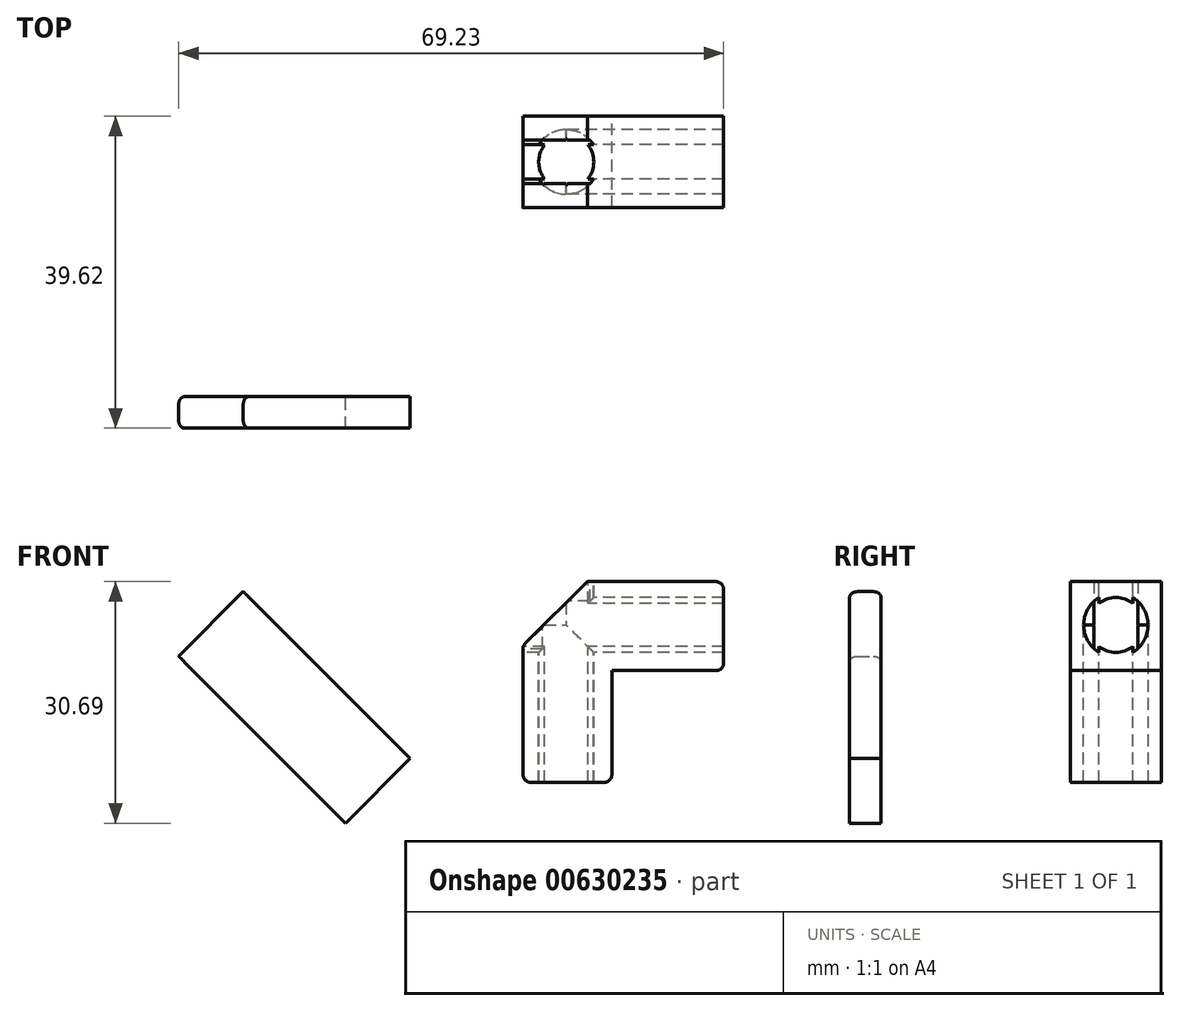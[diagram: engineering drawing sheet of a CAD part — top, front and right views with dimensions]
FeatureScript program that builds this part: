
annotation { "Feature Type Name" : "Feature", "Feature Type Description" : "" }
export const myFeature = defineFeature(function(context is Context, id is Id, definition is map)
    precondition{}
    {
        {
            assignVariable(context, id + "F0", {"name" : "DA", "anyValue" : 7.6});
        }
        {
            assignVariable(context, id + "F1", {"name" : "DH", "anyValue" : 50});
        }
        {
            assignVariable(context, id + "F2", {"name" : "H", "anyValue" : 6});
        }
        {
            assignVariable(context, id + "F3", {"name" : "T", "anyValue" : 2});
        }
        {
            assignVariable(context, id + "F4", {"name" : "WE", "anyValue" : 1.4});
        }
        {
            assignVariable(context, id + "F5", {"name" : "LE", "anyValue" : 60});
        }
        {
            var Q0;
            Q0=qCreatedBy(makeId("Top.planeOp"),FACE);
            var sketch = newSketch(context, id + "F6", { "sketchPlane" : qUnion([Q0])});
            skCircle(sketch, "E0", {"center": v(0, 0) * mm, "radius": 20 * mm});
            skCircle(sketch, "E1", {"center": v(0, 0) * mm, "radius": 3.8 * mm});
            skPoint(sketch, "E2", {"position": v(45, 0) * mm});
            skLineSegment(sketch, "E3", {"start": v(45, -11.85) * mm, "end": v(45, 11.85) * mm, "construction": true});
            skSolve(sketch);
        }
        {
            var Q0;
            Q0=makeQuery(id+"F6.imprint","IMPRINT",FACE,{"disambiguationData":[TD([[makeQuery(id+"F6.imprint","IMPRINT",EDGE,{"derivedFrom":sQuery(id+"F6.wireOp",EDGE,"E0")}),1.0]])]});
            extrude(context, id + "F7", {"entities" : qUnion([Q0]), "endBound" : BoundingType.SYMMETRIC, "depth" : 3 * getVariable(context, 'H') * mm, "offsetDistance" : 25 * mm});
        }
        {
            var Q0;
            Q0=makeQuery(id+"F7.opExtrude","SWEPT_BODY",BODY,{"disambiguationData":[OSD([sQuery(id+"F6.wireOp",EDGE,"E0"),sQuery(id+"F6.wireOp",EDGE,"E1")])]});
            var Q1;
            Q1=sQuery(id+"F6.wireOp",EDGE,"E3");
            circularPattern(context, id + "F8", {"entities" : qUnion([Q0]), "axis" : qUnion([Q1]), "angle" : 360 * degree, "instanceCount" : 4, "equalSpace" : true});
        }
        {
            var Q0;
            Q0=qCreatedBy(makeId("Front.planeOp"),FACE);
            var sketch = newSketch(context, id + "F9", { "sketchPlane" : qUnion([Q0])});
            skPoint(sketch, "E4.0", {"position": v(45, 0) * mm});
            skLineSegment(sketch, "E5.bottom", {"start": v(36, -9) * mm, "end": v(54, -9) * mm, "construction": true});
            skLineSegment(sketch, "E5.top", {"start": v(36, 9) * mm, "end": v(54, 9) * mm, "construction": true});
            skLineSegment(sketch, "E5.left", {"start": v(36, -9) * mm, "end": v(36, 9) * mm, "construction": true});
            skLineSegment(sketch, "E5.right", {"start": v(54, -9) * mm, "end": v(54, 9) * mm, "construction": true});
            skLineSegment(sketch, "E6", {"start": v(16, 29) * mm, "end": v(74, 29) * mm, "construction": true});
            skPoint(sketch, "E7", {"position": v(45, 29) * mm});
            skLineSegment(sketch, "E8", {"start": v(16, 45) * mm, "end": v(74, 45) * mm, "construction": true});
            skPoint(sketch, "E9", {"position": v(45, 45) * mm});
            skLineSegment(sketch, "E10", {"start": v(45, 0) * mm, "end": v(0, 45) * mm, "construction": true});
            skCircle(sketch, "E11", {"center": v(0, 45) * mm, "radius": 3.8 * mm, "construction": true});
            skLineSegment(sketch, "E12", {"start": v(0, 45) * mm, "end": v(-7.03, 52.03) * mm, "construction": true});
            skPoint(sketch, "E13", {"position": v(19.5, 29) * mm});
            skLineSegment(sketch, "E14", {"start": v(19.5, 29) * mm, "end": v(70.5, 29) * mm});
            skLineSegment(sketch, "E15", {"start": v(70.5, 29) * mm, "end": v(70.5, 32.5) * mm});
            skLineSegment(sketch, "E16", {"start": v(70.5, 32.5) * mm, "end": v(19.5, 32.5) * mm});
            skLineSegment(sketch, "E17", {"start": v(19.5, 32.5) * mm, "end": v(19.5, 29) * mm});
            skLineSegment(sketch, "E18", {"start": v(36, 29) * mm, "end": v(36, 23.2) * mm});
            skLineSegment(sketch, "E19", {"start": v(36, 23.2) * mm, "end": v(21.8, 23.2) * mm});
            skLineSegment(sketch, "E20", {"start": v(21.8, 23.2) * mm, "end": v(21.8, 9) * mm});
            skLineSegment(sketch, "E21", {"start": v(21.8, 9) * mm, "end": v(16, 9) * mm});
            skLineSegment(sketch, "E22", {"start": v(36, 32.5) * mm, "end": v(36, 34.5) * mm});
            skLineSegment(sketch, "E23", {"start": v(36, 34.5) * mm, "end": v(10.5, 34.5) * mm});
            skLineSegment(sketch, "E24", {"start": v(10.5, 34.5) * mm, "end": v(10.5, 9) * mm});
            skLineSegment(sketch, "E25", {"start": v(10.5, 9) * mm, "end": v(12.5, 9) * mm});
            skLineSegment(sketch, "E26", {"start": v(12.5, 9) * mm, "end": v(16, 9) * mm});
            skLineSegment(sketch, "E27", {"start": v(36, 29) * mm, "end": v(36, 32.5) * mm});
            skLineSegment(sketch, "E28", {"start": v(16, 29) * mm, "end": v(19.5, 32.5) * mm});
            skLineSegment(sketch, "E29", {"start": v(16, 29) * mm, "end": v(19.5, 29) * mm});
            skLineSegment(sketch, "E30", {"start": v(70.5, 29) * mm, "end": v(74, 29) * mm});
            skLineSegment(sketch, "E31", {"start": v(74, 29) * mm, "end": v(70.5, 32.5) * mm});
            skLineSegment(sketch, "E32", {"start": v(10.5, 26.33) * mm, "end": v(18.67, 34.5) * mm});
            skPoint(sketch, "E33", {"position": v(14.59, 30.41) * mm});
            skSolve(sketch);
        }
        {
            var Q0;
            {var subQ0=sQuery(id+"F9.wireOp",EDGE,"E17");Q0=makeQuery(id+"F9.imprint","IMPRINT",FACE,{"disambiguationData":[TD([[makeQuery(id+"F9.imprint","IMPRINT",EDGE,{"derivedFrom":subQ0}),1.0]])]});}
            var Q1;
            {var subQ0=sQuery(id+"F9.wireOp",EDGE,"E15");Q1=makeQuery(id+"F9.imprint","IMPRINT",FACE,{"disambiguationData":[TD([[makeQuery(id+"F9.imprint","IMPRINT",EDGE,{"derivedFrom":subQ0}),1.0]])]});}
            var Q2;
            Q2=makeQuery(id+"F9.imprint","IMPRINT",FACE,{"disambiguationData":[TD([[makeQuery(id+"F9.imprint","IMPRINT",EDGE,{"derivedFrom":sQuery(id+"F9.wireOp",EDGE,"E17")}),-1.0]])]});
            var Q3;
            Q3=makeQuery(id+"F9.imprint","IMPRINT",FACE,{"disambiguationData":[TD([[makeQuery(id+"F9.imprint","IMPRINT",EDGE,{"derivedFrom":sQuery(id+"F9.wireOp",EDGE,"E15")}),-1.0]])]});
            var Q4;
            Q4=sQuery(id+"F9.wireOp",EDGE,"E6");
            revolve(context, id + "F10", {"entities" : qUnion([Q0, Q1, Q2, Q3]), "axis" : qUnion([Q4]), "revolveType" : RevolveType.FULL});
        }
        {
            var Q0;
            Q0=makeQuery(id+"F10.opRevolve","SWEPT_BODY",BODY,{"disambiguationData":[OSD([sQuery(id+"F9.wireOp",EDGE,"E14"),sQuery(id+"F9.wireOp",EDGE,"E15"),sQuery(id+"F9.wireOp",EDGE,"E16"),sQuery(id+"F9.wireOp",EDGE,"E17")])]});
            transform(context, id + "F11", {"entities" : qUnion([Q0]), "transformType" : TransformType.TRANSLATION_3D, "dx" : 0 * mm, "dy" : 0 * mm, "dz" : (getVariable(context, 'DH') - 3 * getVariable(context, 'H')) / 2 * mm, "makeCopy" : false});
        }
        {
            var Q0;
            {var subQ1=sQuery(id+"F9.wireOp",EDGE,"E17");Q0=makeQuery(id+"F9.imprint","IMPRINT",FACE,{"disambiguationData":[TD([[makeQuery(id+"F9.imprint","IMPRINT",EDGE,{"derivedFrom":subQ1}),-1.0]])]});}
            var Q1;
            {var subQ0=sQuery(id+"F9.wireOp",EDGE,"E17");Q1=makeQuery(id+"F9.imprint","IMPRINT",FACE,{"disambiguationData":[TD([[makeQuery(id+"F9.imprint","IMPRINT",EDGE,{"derivedFrom":subQ0}),1.0]])]});}
            var Q2;
            {var subQ5=sQuery(id+"F9.wireOp",EDGE,"E18");Q2=makeQuery(id+"F9.imprint","IMPRINT",FACE,{"disambiguationData":[TD([[makeQuery(id+"F9.imprint","IMPRINT",EDGE,{"derivedFrom":subQ5}),-1.0]])]});}
            extrude(context, id + "F12", {"entities" : qUnion([Q0, Q1, Q2]), "endBound" : BoundingType.SYMMETRIC, "depth" : (getVariable(context, 'DA') + 2 * 2) * mm, "offsetDistance" : 25 * mm});
        }
        {
            var Q0;
            Q0=makeQuery(id+"F12.opExtrude","SWEPT_BODY",BODY,{"disambiguationData":[OSD([sQuery(id+"F9.wireOp",EDGE,"E18"),sQuery(id+"F9.wireOp",EDGE,"E19"),sQuery(id+"F9.wireOp",EDGE,"E20"),sQuery(id+"F9.wireOp",EDGE,"E21"),sQuery(id+"F9.wireOp",EDGE,"E22"),sQuery(id+"F9.wireOp",EDGE,"E23"),sQuery(id+"F9.wireOp",EDGE,"E24"),sQuery(id+"F9.wireOp",EDGE,"E25"),sQuery(id+"F9.wireOp",EDGE,"E26"),sQuery(id+"F9.wireOp",EDGE,"E27")])]});
            transform(context, id + "F13", {"entities" : qUnion([Q0]), "transformType" : TransformType.TRANSLATION_3D, "dx" : -(getVariable(context, 'DH') - 3 * getVariable(context, 'H')) / 2 * mm, "dy" : 0 * mm, "dz" : (getVariable(context, 'DH') - 3 * getVariable(context, 'H')) / 2 * mm, "makeCopy" : false});
        }
        {
            var Q0;
            Q0=qCreatedBy(makeId("Front.planeOp"),FACE);
            var sketch = newSketch(context, id + "F14", { "sketchPlane" : qUnion([Q0])});
            skLineSegment(sketch, "E34", {"start": v(43, 41.5) * mm, "end": v(47, 41.5) * mm});
            skPoint(sketch, "E35", {"position": v(45, 41.5) * mm});
            skLineSegment(sketch, "E36", {"start": v(45, 41.5) * mm, "end": v(45, 40.7) * mm, "construction": true});
            skArc(sketch, "E37", {"start": v(43, 41.5) * mm, "mid": v(45, 40.7) * mm, "end": v(47, 41.5) * mm});
            skLineSegment(sketch, "E38", {"start": v(70.5, 41.5) * mm, "end": v(19.5, 41.5) * mm, "construction": true});
            skLineSegment(sketch, "E39", {"start": v(19.5, 48.5) * mm, "end": v(70.5, 48.5) * mm, "construction": true});
            skLineSegment(sketch, "E40", {"start": v(45, 41.5) * mm, "end": v(45, 48.5) * mm, "construction": true});
            skPoint(sketch, "E41", {"position": v(45, 45) * mm});
            skLineSegment(sketch, "E42", {"start": v(45, 45) * mm, "end": v(39.35, 45) * mm, "construction": true});
            skSolve(sketch);
        }
        {
            var Q0;
            Q0=makeQuery(id+"F14.imprint","IMPRINT",FACE,{"disambiguationData":[TD([[makeQuery(id+"F14.imprint","IMPRINT",EDGE,{"derivedFrom":sQuery(id+"F14.wireOp",EDGE,"E34")}),-1.0]])]});
            var Q1;
            Q1=sQuery(id+"F14.wireOp",EDGE,"E42");
            revolve(context, id + "F15", {"operationType" : NewBodyOperationType.ADD, "entities" : qUnion([Q0]), "axis" : qUnion([Q1]), "revolveType" : RevolveType.FULL});
        }
        {
            var Q0;
            Q0=qCreatedBy(makeId("Right.planeOp"),FACE);
            var sketch = newSketch(context, id + "F16", { "sketchPlane" : qUnion([Q0])});
            skLineSegment(sketch, "E43.0.0", {"start": v(5.8, 39.2) * mm, "end": v(5.8, 50.5) * mm, "construction": true});
            skLineSegment(sketch, "E43.0.1", {"start": v(5.8, 50.5) * mm, "end": v(-5.8, 50.5) * mm, "construction": true});
            skLineSegment(sketch, "E43.0.2", {"start": v(-5.8, 50.5) * mm, "end": v(-5.8, 39.2) * mm, "construction": true});
            skLineSegment(sketch, "E43.0.3", {"start": v(-5.8, 39.2) * mm, "end": v(5.8, 39.2) * mm, "construction": true});
            skCircle(sketch, "E44.0", {"center": v(0, 45) * mm, "radius": 3.5 * mm, "construction": true});
            skLineSegment(sketch, "E45.bottom", {"start": v(-2.17, 42.26) * mm, "end": v(2.17, 42.26) * mm, "construction": true});
            skLineSegment(sketch, "E45.top", {"start": v(-2.17, 47.74) * mm, "end": v(2.17, 47.74) * mm, "construction": true});
            skLineSegment(sketch, "E45.left", {"start": v(-2.17, 42.26) * mm, "end": v(-2.17, 47.74) * mm, "construction": true});
            skLineSegment(sketch, "E45.right", {"start": v(2.17, 42.26) * mm, "end": v(2.17, 47.74) * mm, "construction": true});
            skLineSegment(sketch, "E46", {"start": v(2.17, 42.26) * mm, "end": v(0, 45) * mm, "construction": true});
            skLineSegment(sketch, "E47", {"start": v(-2.17, 42.26) * mm, "end": v(-2.17, 47.74) * mm});
            skArc(sketch, "E48", {"start": v(-2.17, 47.74) * mm, "mid": v(0, 48.5) * mm, "end": v(2.17, 47.74) * mm});
            skLineSegment(sketch, "E49", {"start": v(2.17, 47.74) * mm, "end": v(2.17, 42.26) * mm});
            skArc(sketch, "E50", {"start": v(2.17, 42.26) * mm, "mid": v(0, 41.5) * mm, "end": v(-2.17, 42.26) * mm});
            skLineSegment(sketch, "E51", {"start": v(-2.77, 41.98) * mm, "end": v(-2.77, 48.02) * mm});
            skPoint(sketch, "E52", {"position": v(-2.77, 45) * mm});
            skLineSegment(sketch, "E53", {"start": v(2.77, 41.98) * mm, "end": v(2.77, 48.02) * mm});
            skLineSegment(sketch, "E54", {"start": v(2.77, 48.02) * mm, "end": v(-2.77, 48.02) * mm, "construction": true});
            skLineSegment(sketch, "E55", {"start": v(-2.77, 41.98) * mm, "end": v(2.77, 41.98) * mm, "construction": true});
            skPoint(sketch, "E56", {"position": v(0, 48.02) * mm});
            skArc(sketch, "E57", {"start": v(-2.78, 48.02) * mm, "mid": v(0, 49.1) * mm, "end": v(2.78, 48.02) * mm});
            skArc(sketch, "E58", {"start": v(-2.78, 41.98) * mm, "mid": v(0, 40.9) * mm, "end": v(2.78, 41.98) * mm});
            skPoint(sketch, "E59", {"position": v(0, 48.5) * mm});
            skPoint(sketch, "E60", {"position": v(0, 49.1) * mm});
            skArc(sketch, "E61", {"start": v(-2.78, 41.98) * mm, "mid": v(-4.1, 45) * mm, "end": v(-2.78, 48.02) * mm});
            skArc(sketch, "E62", {"start": v(2.78, 48.02) * mm, "mid": v(4.1, 45) * mm, "end": v(2.78, 41.98) * mm});
            skCircle(sketch, "E63", {"center": v(0, 45) * mm, "radius": 4.3 * mm, "construction": true});
            skLineSegment(sketch, "E64", {"start": v(-2.17, 42.26) * mm, "end": v(-2.17, 41.3) * mm});
            skLineSegment(sketch, "E65", {"start": v(-2.17, 47.74) * mm, "end": v(-2.17, 48.7) * mm});
            skLineSegment(sketch, "E66", {"start": v(2.17, 42.26) * mm, "end": v(2.17, 41.3) * mm});
            skLineSegment(sketch, "E67", {"start": v(2.17, 47.74) * mm, "end": v(2.17, 48.7) * mm});
            skArc(sketch, "E68", {"start": v(-2.18, 41.3) * mm, "mid": v(-4.3, 45) * mm, "end": v(-2.18, 48.7) * mm});
            skArc(sketch, "E69", {"start": v(2.18, 41.3) * mm, "mid": v(4.3, 45) * mm, "end": v(2.18, 48.7) * mm});
            skSolve(sketch);
        }
        {
            var Q0;
            Q0=makeQuery(id+"F16.imprint","IMPRINT",FACE,{"disambiguationData":[TD([[makeQuery(id+"F16.imprint","IMPRINT",EDGE,{"derivedFrom":sQuery(id+"F16.wireOp",EDGE,"E53")}),-1.0]])]});
            var Q1;
            Q1=makeQuery(id+"F16.imprint","IMPRINT",FACE,{"disambiguationData":[TD([[makeQuery(id+"F16.imprint","IMPRINT",EDGE,{"derivedFrom":sQuery(id+"F16.wireOp",EDGE,"E51")}),1.0]])]});
            var Q2;
            Q2=makeQuery(id+"F16.imprint","IMPRINT",FACE,{"disambiguationData":[TD([[makeQuery(id+"F16.imprint","IMPRINT",EDGE,{"derivedFrom":sQuery(id+"F16.wireOp",EDGE,"E47")}),1.0]])]});
            var Q3;
            {var subQ4=sQuery(id+"F16.wireOp",EDGE,"E61");Q3=makeQuery(id+"F16.imprint","IMPRINT",FACE,{"disambiguationData":[TD([[makeQuery(id+"F16.imprint","IMPRINT",EDGE,{"derivedFrom":subQ4}),1.0]])]});}
            var Q4;
            {var subQ4=sQuery(id+"F16.wireOp",EDGE,"E62");Q4=makeQuery(id+"F16.imprint","IMPRINT",FACE,{"disambiguationData":[TD([[makeQuery(id+"F16.imprint","IMPRINT",EDGE,{"derivedFrom":subQ4}),1.0]])]});}
            var Q5;
            {var subQ8=sQuery(id+"F16.wireOp",EDGE,"E49");Q5=makeQuery(id+"F16.imprint","IMPRINT",FACE,{"disambiguationData":[TD([[makeQuery(id+"F16.imprint","IMPRINT",EDGE,{"derivedFrom":subQ8}),1.0]])]});}
            extrude(context, id + "F17", {"entities" : qUnion([Q0, Q1, Q2, Q3, Q4, Q5]), "operationType" : NewBodyOperationType.REMOVE, "endBound" : BoundingType.THROUGH_ALL, "depth" : 25 * mm, "offsetDistance" : 25 * mm});
        }
        {
            var Q0;
            Q0=makeQuery(id+"F17.boolean.opBoolean","COPY",FACE,{"derivedFrom":makeQuery(id+"F17.opExtrude","SWEPT_FACE",FACE,{"disambiguationData":[OSD([sQuery(id+"F16.wireOp",EDGE,"E47")])]})});
            var sketch = newSketch(context, id + "F18", { "sketchPlane" : qUnion([Q0])});
            skPoint(sketch, "E70", {"position": v(45, 47.74) * mm});
            skLineSegment(sketch, "E71", {"start": v(45, 42.26) * mm, "end": v(45, 47.74) * mm, "construction": true});
            skPoint(sketch, "E72", {"position": v(45, 45) * mm});
            skLineSegment(sketch, "E73.bottom", {"start": v(54, 43.6) * mm, "end": v(36, 43.6) * mm});
            skLineSegment(sketch, "E73.top", {"start": v(54, 46.4) * mm, "end": v(36, 46.4) * mm});
            skLineSegment(sketch, "E73.left", {"start": v(54, 43.6) * mm, "end": v(54, 46.4) * mm, "construction": true});
            skLineSegment(sketch, "E73.right", {"start": v(36, 43.6) * mm, "end": v(36, 46.4) * mm, "construction": true});
            skArc(sketch, "E74", {"start": v(36, 43.6) * mm, "mid": v(34.6, 45) * mm, "end": v(36, 46.4) * mm});
            skArc(sketch, "E75", {"start": v(54, 43.6) * mm, "mid": v(55.4, 45) * mm, "end": v(54, 46.4) * mm});
            skArc(sketch, "E76", {"start": v(31.59, 45) * mm, "mid": v(31.18, 44.01) * mm, "end": v(30.19, 43.6) * mm});
            skArc(sketch, "E77", {"start": v(31.59, 45) * mm, "mid": v(32.04, 46.95) * mm, "end": v(33.31, 48.5) * mm});
            skLineSegment(sketch, "E78", {"start": v(30.19, 43.6) * mm, "end": v(20.98, 43.6) * mm});
            skArc(sketch, "E79", {"start": v(20.98, 43.6) * mm, "mid": v(19.58, 45) * mm, "end": v(20.98, 46.4) * mm});
            skLineSegment(sketch, "E80", {"start": v(20.98, 46.4) * mm, "end": v(30.19, 46.4) * mm});
            skArc(sketch, "E81", {"start": v(30.19, 46.4) * mm, "mid": v(30.57, 47.5) * mm, "end": v(31.15, 48.5) * mm});
            skPoint(sketch, "E82", {"position": v(19.58, 45) * mm});
            skFitSpline(sketch, "E83.0", {"points": [v(33.05, 28.1) * mm, v(32.15, 29) * mm, v(30.36, 30.8) * mm, v(28.12, 33.08) * mm, v(26.33, 34.9) * mm, v(25, 36.27) * mm, v(23.67, 37.64) * mm, v(22.35, 39.03) * mm, v(21.27, 40.2) * mm, v(20.42, 41.15) * mm, v(19.8, 41.88) * mm, v(19.2, 42.63) * mm, v(18.75, 43.29) * mm, v(18.45, 43.85) * mm, v(18.3, 44.23) * mm, v(18.22, 44.54) * mm, v(18.18, 44.78) * mm, v(18.17, 45.02) * mm, v(18.19, 45.25) * mm, v(18.23, 45.5) * mm, v(18.31, 45.8) * mm, v(18.46, 46.17) * mm, v(18.69, 46.6) * mm, v(19.04, 47.13) * mm, v(19.51, 47.77) * mm, v(20.12, 48.5) * mm, v(20.75, 49.23) * mm, v(21.6, 50.17) * mm, v(22.25, 50.87) * mm, v(22.7, 51.33) * mm], "construction": true});
            skPoint(sketch, "E84", {"position": v(18.18, 45) * mm});
            skLineSegment(sketch, "E85.MirrorCS", {"start": v(59.81, 43.6) * mm, "end": v(69.02, 43.6) * mm});
            skArc(sketch, "E86.MirrorCS", {"start": v(69.02, 43.6) * mm, "mid": v(70.42, 45) * mm, "end": v(69.02, 46.4) * mm});
            skArc(sketch, "E87.MirrorCS", {"start": v(59.81, 46.4) * mm, "mid": v(59.43, 47.5) * mm, "end": v(58.85, 48.5) * mm});
            skArc(sketch, "E88.MirrorCS", {"start": v(58.41, 45) * mm, "mid": v(57.96, 46.95) * mm, "end": v(56.69, 48.5) * mm});
            skArc(sketch, "E89.MirrorCS", {"start": v(58.41, 45) * mm, "mid": v(58.82, 44.01) * mm, "end": v(59.81, 43.6) * mm});
            skLineSegment(sketch, "E90", {"start": v(69.02, 46.4) * mm, "end": v(59.81, 46.4) * mm});
            skLineSegment(sketch, "E91", {"start": v(58.85, 48.5) * mm, "end": v(56.69, 48.5) * mm});
            skLineSegment(sketch, "E92.0", {"start": v(43, 47.74) * mm, "end": v(19.5, 47.74) * mm, "construction": true});
            skLineSegment(sketch, "E93.0", {"start": v(70.5, 47.74) * mm, "end": v(47, 47.74) * mm, "construction": true});
            skLineSegment(sketch, "E94.0", {"start": v(19.5, 42.26) * mm, "end": v(43, 42.26) * mm, "construction": true});
            skLineSegment(sketch, "E95.0", {"start": v(47, 42.26) * mm, "end": v(70.5, 42.26) * mm, "construction": true});
            skLineSegment(sketch, "E96", {"start": v(43, 47.74) * mm, "end": v(47, 47.74) * mm, "construction": true});
            skLineSegment(sketch, "E97", {"start": v(43, 42.26) * mm, "end": v(47, 42.26) * mm, "construction": true});
            skLineSegment(sketch, "E98", {"start": v(45, 45) * mm, "end": v(18.18, 45) * mm, "construction": true});
            skLineSegment(sketch, "E99", {"start": v(20.98, 43.6) * mm, "end": v(20.98, 46.4) * mm, "construction": true});
            skLineSegment(sketch, "E100", {"start": v(36, 43.6) * mm, "end": v(18.59, 43.6) * mm, "construction": true});
            skLineSegment(sketch, "E101", {"start": v(36, 46.4) * mm, "end": v(18.59, 46.4) * mm, "construction": true});
            skLineSegment(sketch, "E102", {"start": v(30.19, 43.6) * mm, "end": v(30.19, 46.4) * mm, "construction": true});
            skPoint(sketch, "E103", {"position": v(31.59, 45) * mm});
            skLineSegment(sketch, "E104", {"start": v(19.5, 48.5) * mm, "end": v(42.7, 48.5) * mm, "construction": true});
            skLineSegment(sketch, "E105", {"start": v(31.15, 48.5) * mm, "end": v(33.31, 48.5) * mm});
            skSolve(sketch);
        }
        {
            var Q0;
            {var subQ1=sQuery(id+"F18.wireOp",EDGE,"E76");Q0=makeQuery(id+"F18.imprint","IMPRINT",FACE,{"disambiguationData":[TD([[makeQuery(id+"F18.imprint","IMPRINT",EDGE,{"derivedFrom":subQ1}),-1.0]])]});}
            var Q1;
            Q1=makeQuery(id+"F18.imprint","IMPRINT",FACE,{"disambiguationData":[TD([[makeQuery(id+"F18.imprint","IMPRINT",EDGE,{"derivedFrom":sQuery(id+"F18.wireOp",EDGE,"E73.bottom")}),-1.0]])]});
            var Q2;
            Q2=makeQuery(id+"F18.imprint","IMPRINT",FACE,{"disambiguationData":[TD([[makeQuery(id+"F18.imprint","IMPRINT",EDGE,{"derivedFrom":sQuery(id+"F18.wireOp",EDGE,"E85.MirrorCS")}),1.0]])]});
            var Q3;
            {var subQ0=sQuery(id+"F18.wireOp",EDGE,"E91");Q3=makeQuery(id+"F18.imprint","IMPRINT",FACE,{"disambiguationData":[TD([[makeQuery(id+"F18.imprint","IMPRINT",EDGE,{"derivedFrom":subQ0}),1.0]])]});}
            var Q4;
            {var subQ0=sQuery(id+"F18.wireOp",EDGE,"E105");Q4=makeQuery(id+"F18.imprint","IMPRINT",FACE,{"disambiguationData":[TD([[makeQuery(id+"F18.imprint","IMPRINT",EDGE,{"derivedFrom":subQ0}),-1.0]])]});}
            extrude(context, id + "F19", {"entities" : qUnion([Q0, Q1, Q2, Q3, Q4]), "operationType" : NewBodyOperationType.REMOVE, "oppositeDirection" : true, "depth" : 25 * mm, "offsetDistance" : 25 * mm});
        }
        {
            var Q0;
            Q0=makeQuery(id+"F16.imprint","IMPRINT",FACE,{"disambiguationData":[TD([[makeQuery(id+"F16.imprint","IMPRINT",EDGE,{"derivedFrom":sQuery(id+"F16.wireOp",EDGE,"E47")}),-1.0]])]});
            var Q1;
            {var subQ0=sQuery(id+"F16.wireOp",EDGE,"E50");Q1=makeQuery(id+"F16.imprint","IMPRINT",FACE,{"disambiguationData":[TD([[makeQuery(id+"F16.imprint","IMPRINT",EDGE,{"derivedFrom":subQ0}),1.0]])]});}
            var Q2;
            {var subQ8=sQuery(id+"F16.wireOp",EDGE,"E47");Q2=makeQuery(id+"F16.imprint","IMPRINT",FACE,{"disambiguationData":[TD([[makeQuery(id+"F16.imprint","IMPRINT",EDGE,{"derivedFrom":subQ8}),1.0]])]});}
            var Q3;
            {var subQ8=sQuery(id+"F16.wireOp",EDGE,"E49");Q3=makeQuery(id+"F16.imprint","IMPRINT",FACE,{"disambiguationData":[TD([[makeQuery(id+"F16.imprint","IMPRINT",EDGE,{"derivedFrom":subQ8}),1.0]])]});}
            var Q4;
            {var subQ0=sQuery(id+"F16.wireOp",EDGE,"E48");Q4=makeQuery(id+"F16.imprint","IMPRINT",FACE,{"disambiguationData":[TD([[makeQuery(id+"F16.imprint","IMPRINT",EDGE,{"derivedFrom":subQ0}),1.0]])]});}
            extrude(context, id + "F20", {"entities" : qUnion([Q0, Q1, Q2, Q3, Q4]), "operationType" : NewBodyOperationType.REMOVE, "endBound" : BoundingType.SYMMETRIC, "depth" : 100 * mm, "offsetDistance" : 25 * mm});
        }
        {
            var Q0;
            Q0=makeQuery(id+"F12.opExtrude","CAP_FACE",FACE,{"disambiguationData":[OSD([sQuery(id+"F9.wireOp",EDGE,"E18"),sQuery(id+"F9.wireOp",EDGE,"E19"),sQuery(id+"F9.wireOp",EDGE,"E20"),sQuery(id+"F9.wireOp",EDGE,"E21"),sQuery(id+"F9.wireOp",EDGE,"E22"),sQuery(id+"F9.wireOp",EDGE,"E23"),sQuery(id+"F9.wireOp",EDGE,"E24"),sQuery(id+"F9.wireOp",EDGE,"E25"),sQuery(id+"F9.wireOp",EDGE,"E26"),sQuery(id+"F9.wireOp",EDGE,"E27"),sQuery(id+"F9.wireOp",EDGE,"E32")])],"isStart":false});
            var sketch = newSketch(context, id + "F21", { "sketchPlane" : qUnion([Q0])});
            skLineSegment(sketch, "E106.0", {"start": v(-5.5, 42.33) * mm, "end": v(2.67, 50.5) * mm, "construction": true});
            skPoint(sketch, "E107.0", {"position": v(5.8, 39.2) * mm});
            skLineSegment(sketch, "E108", {"start": v(5.8, 39.2) * mm, "end": v(-1.41, 46.41) * mm, "construction": true});
            skSolve(sketch);
        }
        {
            var Q0;
            Q0=sQuery(id+"F21.wireOp",EDGE,"E108");
            var Q1;
            Q1=sQuery(id+"F21.wireOp",VERTEX,"E106.0.end");
            cPlane(context, id + "F22", {"entities" : qUnion([Q0, Q1]), "cplaneType" : CPlaneType.LINE_ANGLE, "offset" : 25 * mm, "angle" : 90 * degree, "width" : 150 * mm, "height" : 150 * mm});
        }
        {
            var Q0;
            Q0=makeQuery(id+"F12.opExtrude","SWEPT_BODY",BODY,{"disambiguationData":[OSD([sQuery(id+"F9.wireOp",EDGE,"E18"),sQuery(id+"F9.wireOp",EDGE,"E19"),sQuery(id+"F9.wireOp",EDGE,"E20"),sQuery(id+"F9.wireOp",EDGE,"E21"),sQuery(id+"F9.wireOp",EDGE,"E22"),sQuery(id+"F9.wireOp",EDGE,"E23"),sQuery(id+"F9.wireOp",EDGE,"E24"),sQuery(id+"F9.wireOp",EDGE,"E25"),sQuery(id+"F9.wireOp",EDGE,"E26"),sQuery(id+"F9.wireOp",EDGE,"E27"),sQuery(id+"F9.wireOp",EDGE,"E32")])]});
            var Q1;
            Q1=qCreatedBy(id+"F22.planeOp",FACE);
            mirror(context, id + "F23", {"operationType" : NewBodyOperationType.INTERSECT, "entities" : qUnion([Q0]), "mirrorPlane" : qUnion([Q1])});
        }
        {
            var Q0;
            Q0=makeQuery(id+"F17.boolean.opBoolean","COPY",FACE,{"derivedFrom":makeQuery(id+"F17.opExtrude","SWEPT_FACE",FACE,{"disambiguationData":[OSD([sQuery(id+"F16.wireOp",EDGE,"E47"),sQuery(id+"F16.wireOp",EDGE,"E64"),sQuery(id+"F16.wireOp",EDGE,"E65")])]})});
            var sketch = newSketch(context, id + "F24", { "sketchPlane" : qUnion([Q0])});
            skPoint(sketch, "E109.0", {"position": v(45, 45) * mm});
            skFitSpline(sketch, "E110.0", {"points": [v(33.05, 28.1) * mm, v(32.15, 29) * mm, v(30.36, 30.8) * mm, v(28.12, 33.08) * mm, v(26.33, 34.9) * mm, v(25, 36.27) * mm, v(23.67, 37.64) * mm, v(22.35, 39.03) * mm, v(21.27, 40.2) * mm, v(20.42, 41.15) * mm, v(19.8, 41.88) * mm, v(19.2, 42.63) * mm, v(18.75, 43.29) * mm, v(18.45, 43.85) * mm, v(18.3, 44.23) * mm, v(18.22, 44.54) * mm, v(18.18, 44.78) * mm, v(18.17, 45.02) * mm, v(18.19, 45.25) * mm, v(18.23, 45.5) * mm, v(18.31, 45.8) * mm, v(18.46, 46.17) * mm, v(18.69, 46.6) * mm, v(19.04, 47.13) * mm, v(19.51, 47.77) * mm, v(20.12, 48.5) * mm, v(20.75, 49.23) * mm, v(21.6, 50.17) * mm, v(22.25, 50.87) * mm, v(22.7, 51.33) * mm], "construction": true});
            skArc(sketch, "E111.0", {"start": v(20.98, 43.6) * mm, "mid": v(19.58, 45) * mm, "end": v(20.98, 46.4) * mm, "construction": true});
            skArc(sketch, "E112.0", {"start": v(69.02, 43.6) * mm, "mid": v(70.42, 45) * mm, "end": v(69.02, 46.4) * mm, "construction": true});
            skFitSpline(sketch, "E113.0", {"points": [v(56.95, 28.1) * mm, v(57.85, 29) * mm, v(59.64, 30.8) * mm, v(61.88, 33.08) * mm, v(63.67, 34.9) * mm, v(65, 36.27) * mm, v(66.33, 37.64) * mm, v(67.65, 39.03) * mm, v(68.73, 40.2) * mm, v(69.58, 41.15) * mm, v(70.2, 41.88) * mm, v(70.8, 42.63) * mm, v(71.25, 43.29) * mm, v(71.55, 43.85) * mm, v(71.7, 44.23) * mm, v(71.78, 44.54) * mm, v(71.82, 44.78) * mm, v(71.83, 45.02) * mm, v(71.81, 45.25) * mm, v(71.77, 45.5) * mm, v(71.69, 45.8) * mm, v(71.54, 46.17) * mm, v(71.31, 46.6) * mm, v(70.96, 47.13) * mm, v(70.49, 47.77) * mm, v(69.88, 48.5) * mm, v(69.25, 49.23) * mm, v(68.4, 50.17) * mm, v(67.75, 50.87) * mm, v(67.3, 51.33) * mm], "construction": true});
            skLineSegment(sketch, "E114.bottom", {"start": v(70.24, 44.3) * mm, "end": v(74, 44.3) * mm});
            skLineSegment(sketch, "E114.top", {"start": v(70.24, 45.7) * mm, "end": v(74, 45.7) * mm});
            skLineSegment(sketch, "E114.left", {"start": v(70.24, 44.3) * mm, "end": v(70.24, 45.7) * mm});
            skLineSegment(sketch, "E114.right", {"start": v(74, 44.3) * mm, "end": v(74, 45.7) * mm});
            skPoint(sketch, "E115", {"position": v(70.24, 45) * mm});
            skLineSegment(sketch, "E116.0", {"start": v(45, 42.26) * mm, "end": v(45, 47.74) * mm, "construction": true});
            skLineSegment(sketch, "E117.MirrorCS", {"start": v(19.76, 44.3) * mm, "end": v(16, 44.3) * mm});
            skLineSegment(sketch, "E118.MirrorCS", {"start": v(16, 44.3) * mm, "end": v(16, 45.7) * mm});
            skLineSegment(sketch, "E119.MirrorCS", {"start": v(19.76, 45.7) * mm, "end": v(16, 45.7) * mm});
            skLineSegment(sketch, "E120.MirrorCS", {"start": v(19.76, 44.3) * mm, "end": v(19.76, 45.7) * mm});
            skPoint(sketch, "E121.0", {"position": v(74, 45) * mm});
            skSolve(sketch);
        }
        {
            var Q0;
            {var subQ0=sQuery(id+"F24.wireOp",EDGE,"E117.MirrorCS");var subQ4=sQuery(id+"F24.wireOp",EDGE,"E120.MirrorCS");var subQ6=makeQuery(id+"F19.boolean.opBoolean","COPY",EDGE,{"derivedFrom":makeQuery(id+"F19.opExtrude","CAP_EDGE",EDGE,{"disambiguationData":[OSD([sQuery(id+"F18.wireOp",EDGE,"E79")])],"isStart":true})});var subQ9=makeQuery(id+"F24.imprint","INTERSECT",VERTEX,{"derivedFrom":[subQ6,subQ0,subQ4]});Q0=makeQuery(id+"F24.imprint","IMPRINT",FACE,{"disambiguationData":[TD([[makeQuery(id+"F24.imprint","IMPRINT",EDGE,{"disambiguationData":[TD([[subQ9,-1.0]])],"derivedFrom":subQ6}),1.0]])]});}
            var Q1;
            {var subQ0=sQuery(id+"F24.wireOp",EDGE,"E120.MirrorCS");Q1=makeQuery(id+"F24.imprint","IMPRINT",FACE,{"disambiguationData":[TD([[makeQuery(id+"F24.imprint","IMPRINT",EDGE,{"derivedFrom":subQ0}),1.0]])]});}
            var Q2;
            {var subQ0=sQuery(id+"F24.wireOp",EDGE,"E114.bottom");var subQ4=sQuery(id+"F24.wireOp",EDGE,"E114.left");var subQ6=makeQuery(id+"F19.boolean.opBoolean","COPY",EDGE,{"derivedFrom":makeQuery(id+"F19.opExtrude","CAP_EDGE",EDGE,{"disambiguationData":[OSD([sQuery(id+"F18.wireOp",EDGE,"E86.MirrorCS")])],"isStart":true})});var subQ9=makeQuery(id+"F24.imprint","INTERSECT",VERTEX,{"derivedFrom":[subQ6,subQ0,subQ4]});Q2=makeQuery(id+"F24.imprint","IMPRINT",FACE,{"disambiguationData":[TD([[makeQuery(id+"F24.imprint","IMPRINT",EDGE,{"disambiguationData":[TD([[subQ9,-1.0]])],"derivedFrom":subQ6}),-1.0]])]});}
            var Q3;
            {var subQ0=sQuery(id+"F24.wireOp",EDGE,"E114.left");Q3=makeQuery(id+"F24.imprint","IMPRINT",FACE,{"disambiguationData":[TD([[makeQuery(id+"F24.imprint","IMPRINT",EDGE,{"derivedFrom":subQ0}),-1.0]])]});}
            var Q4;
            {var subQ0=sQuery(id+"F24.wireOp",EDGE,"E114.right");Q4=makeQuery(id+"F24.imprint","IMPRINT",FACE,{"disambiguationData":[TD([[makeQuery(id+"F24.imprint","IMPRINT",EDGE,{"derivedFrom":subQ0}),1.0]])]});}
            var Q5;
            {var subQ0=sQuery(id+"F24.wireOp",EDGE,"E118.MirrorCS");Q5=makeQuery(id+"F24.imprint","IMPRINT",FACE,{"disambiguationData":[TD([[makeQuery(id+"F24.imprint","IMPRINT",EDGE,{"derivedFrom":subQ0}),-1.0]])]});}
            extrude(context, id + "F25", {"entities" : qUnion([Q0, Q1, Q2, Q3, Q4, Q5]), "operationType" : NewBodyOperationType.REMOVE, "oppositeDirection" : true, "depth" : getVariable(context, 'WE') * mm, "offsetDistance" : 25 * mm});
        }
        {
            var Q0;
            Q0=makeQuery(id+"F17.boolean.opBoolean","COPY",FACE,{"derivedFrom":makeQuery(id+"F17.opExtrude","SWEPT_FACE",FACE,{"disambiguationData":[OSD([sQuery(id+"F16.wireOp",EDGE,"E49"),sQuery(id+"F16.wireOp",EDGE,"E66"),sQuery(id+"F16.wireOp",EDGE,"E67")])]})});
            var sketch = newSketch(context, id + "F26", { "sketchPlane" : qUnion([Q0])});
            skLineSegment(sketch, "E122.0.0", {"start": v(-17.04, 44.3) * mm, "end": v(-19.76, 44.3) * mm});
            skArc(sketch, "E122.0.1", {"start": v(-19.76, 44.3) * mm, "mid": v(-19.58, 45) * mm, "end": v(-19.76, 45.7) * mm});
            skLineSegment(sketch, "E122.0.2", {"start": v(-19.76, 45.7) * mm, "end": v(-17.04, 45.7) * mm});
            skFitSpline(sketch, "E122.0.3", {"points": [v(-17.28, 45.5) * mm, v(-17.25, 45.42) * mm, v(-17.2, 45.26) * mm, v(-17.16, 44.91) * mm, v(-17.21, 44.66) * mm, v(-17.28, 44.5) * mm]});
            skLineSegment(sketch, "E123.0", {"start": v(-19.76, 44.3) * mm, "end": v(-16, 44.3) * mm});
            skLineSegment(sketch, "E124.0", {"start": v(-19.76, 45.7) * mm, "end": v(-16, 45.7) * mm});
            skLineSegment(sketch, "E125.0", {"start": v(-16, 44.3) * mm, "end": v(-16, 45.7) * mm});
            skLineSegment(sketch, "E126.0", {"start": v(-70.24, 44.3) * mm, "end": v(-74, 44.3) * mm});
            skLineSegment(sketch, "E127.0", {"start": v(-74, 44.3) * mm, "end": v(-74, 45.7) * mm});
            skLineSegment(sketch, "E128.0", {"start": v(-70.24, 45.7) * mm, "end": v(-74, 45.7) * mm});
            skLineSegment(sketch, "E129.0", {"start": v(-70.24, 44.3) * mm, "end": v(-70.24, 45.7) * mm});
            skSolve(sketch);
        }
        {
            var Q0;
            {var subQ0=sQuery(id+"F26.wireOp",EDGE,"E122.0.3");Q0=makeQuery(id+"F26.imprint","IMPRINT",FACE,{"disambiguationData":[TD([[makeQuery(id+"F26.imprint","IMPRINT",EDGE,{"derivedFrom":subQ0}),1.0]])]});}
            var Q1;
            {var subQ0=sQuery(id+"F26.wireOp",EDGE,"E127.0");Q1=makeQuery(id+"F26.imprint","IMPRINT",FACE,{"disambiguationData":[TD([[makeQuery(id+"F26.imprint","IMPRINT",EDGE,{"derivedFrom":subQ0}),-1.0]])]});}
            var Q2;
            {var subQ1=sQuery(id+"F26.wireOp",EDGE,"E126.0");var subQ2=makeQuery(id+"F17.opExtrude","SWEPT_FACE",FACE,{"disambiguationData":[OSD([sQuery(id+"F16.wireOp",EDGE,"E53")])]});var subQ5=makeQuery(id+"F17.boolean.opBoolean","INTERSECT",EDGE,{"derivedFrom":[makeQuery(id+"F10.opRevolve","SWEPT_FACE",FACE,{"disambiguationData":[OSD([sQuery(id+"F9.wireOp",EDGE,"E31")])]}),subQ2]});var subQ6=makeQuery(id+"F26.imprint","INTERSECT",VERTEX,{"derivedFrom":[subQ5,subQ1]});Q2=makeQuery(id+"F26.imprint","IMPRINT",FACE,{"disambiguationData":[TD([[makeQuery(id+"F26.imprint","IMPRINT",EDGE,{"disambiguationData":[TD([[subQ6,1.0]])],"derivedFrom":subQ1}),-1.0]])]});}
            var Q3;
            {var subQ0=sQuery(id+"F26.wireOp",EDGE,"E122.0.1");Q3=makeQuery(id+"F26.imprint","IMPRINT",FACE,{"disambiguationData":[TD([[makeQuery(id+"F26.imprint","IMPRINT",EDGE,{"derivedFrom":subQ0}),-1.0]])]});}
            var Q4;
            {var subQ0=sQuery(id+"F26.wireOp",EDGE,"E122.0.3");Q4=makeQuery(id+"F26.imprint","IMPRINT",FACE,{"disambiguationData":[TD([[makeQuery(id+"F26.imprint","IMPRINT",EDGE,{"derivedFrom":subQ0}),-1.0]])]});}
            extrude(context, id + "F27", {"entities" : qUnion([Q0, Q1, Q2, Q3, Q4]), "operationType" : NewBodyOperationType.REMOVE, "oppositeDirection" : true, "depth" : getVariable(context, 'WE') * mm, "offsetDistance" : 25 * mm});
        }
        {
            var Q0;
            {var subQ0=makeQuery(id+"F20.boolean.opBoolean","COPY",FACE,{"derivedFrom":makeQuery(id+"F20.opExtrude","SWEPT_FACE",FACE,{"disambiguationData":[OSD([sQuery(id+"F16.wireOp",EDGE,"E51")])]})});var subQ3=sQuery(id+"F9.wireOp",EDGE,"E32");Q0=makeQuery(id+"F23.boolean.opBoolean","SPLIT",FACE,{"disambiguationData":[TD([subQ0])],"derivedFrom":makeQuery(id+"F12.opExtrude","SWEPT_FACE",FACE,{"disambiguationData":[OSD([subQ3])]})});}
            var sketch = newSketch(context, id + "F28", { "sketchPlane" : qUnion([Q0])});
            skPoint(sketch, "E130", {"position": v(31.82, -5.8) * mm});
            skLineSegment(sketch, "E131", {"start": v(33.82, -5.8) * mm, "end": v(29.82, -5.8) * mm});
            skLineSegment(sketch, "E132.0", {"start": v(26.04, 5.8) * mm, "end": v(37.6, 5.8) * mm, "construction": true});
            skLineSegment(sketch, "E133", {"start": v(33.82, -5.8) * mm, "end": v(33.82, 5.8) * mm});
            skLineSegment(sketch, "E134", {"start": v(33.82, 5.8) * mm, "end": v(29.82, 5.8) * mm});
            skLineSegment(sketch, "E135", {"start": v(29.82, 5.8) * mm, "end": v(29.82, -5.8) * mm});
            skSolve(sketch);
        }
        {
            var Q0;
            {var subQ0=sQuery(id+"F28.wireOp",EDGE,"E134");Q0=makeQuery(id+"F28.imprint","IMPRINT",FACE,{"disambiguationData":[TD([[makeQuery(id+"F28.imprint","IMPRINT",EDGE,{"derivedFrom":subQ0}),1.0]])]});}
            var Q1;
            {var subQ0=sQuery(id+"F28.wireOp",EDGE,"E131");Q1=makeQuery(id+"F28.imprint","IMPRINT",FACE,{"disambiguationData":[TD([[makeQuery(id+"F28.imprint","IMPRINT",EDGE,{"derivedFrom":subQ0}),1.0]])]});}
            extrude(context, id + "F29", {"entities" : qUnion([Q0, Q1]), "operationType" : NewBodyOperationType.ADD, "depth" : getVariable(context, 'LE') / 2 * mm, "offsetDistance" : 25 * mm});
        }
        {
            var Q0;
            Q0=makeQuery(id+"F29.opExtrude","SWEPT_FACE",FACE,{"disambiguationData":[OSD([sQuery(id+"F28.wireOp",EDGE,"E133")])]});
            var sketch = newSketch(context, id + "F30", { "sketchPlane" : qUnion([Q0])});
            skPoint(sketch, "E136", {"position": v(0, 63.82) * mm});
            skLineSegment(sketch, "E137", {"start": v(0, 63.82) * mm, "end": v(0, 48.8) * mm, "construction": true});
            skLineSegment(sketch, "E138", {"start": v(0, 59.84) * mm, "end": v(-3.98, 63.82) * mm});
            skLineSegment(sketch, "E139", {"start": v(-3.98, 63.82) * mm, "end": v(-2, 63.82) * mm});
            skLineSegment(sketch, "E140", {"start": v(-2, 63.82) * mm, "end": v(0, 61.82) * mm});
            skLineSegment(sketch, "E141", {"start": v(0, 61.82) * mm, "end": v(0, 59.84) * mm});
            skArc(sketch, "E142", {"start": v(-0.99, 60.83) * mm, "mid": v(-0.54, 60.53) * mm, "end": v(0, 60.42) * mm});
            skArc(sketch, "E143", {"start": v(-0.99, 60.83) * mm, "mid": v(0, 60.42) * mm, "end": v(0.99, 60.83) * mm});
            skLineSegment(sketch, "E144", {"start": v(0, 61.82) * mm, "end": v(0.99, 60.83) * mm});
            skSolve(sketch);
        }
        {
            var Q0;
            {var subQ3=sQuery(id+"F30.wireOp",EDGE,"E139");Q0=makeQuery(id+"F30.imprint","IMPRINT",FACE,{"disambiguationData":[TD([[makeQuery(id+"F30.imprint","IMPRINT",EDGE,{"derivedFrom":subQ3}),-1.0]])]});}
            var Q1;
            {var subQ0=sQuery(id+"F30.wireOp",EDGE,"E144");Q1=makeQuery(id+"F30.imprint","IMPRINT",FACE,{"disambiguationData":[TD([[makeQuery(id+"F30.imprint","IMPRINT",EDGE,{"derivedFrom":subQ0}),-1.0]])]});}
            extrude(context, id + "F31", {"entities" : qUnion([Q0, Q1]), "operationType" : NewBodyOperationType.REMOVE, "endBound" : BoundingType.THROUGH_ALL, "oppositeDirection" : true, "depth" : 25 * mm, "offsetDistance" : 25 * mm});
        }
        {
            var Q0;
            {var subQ0=sQuery(id+"F28.wireOp",EDGE,"E133");var subQ1=sQuery(id+"F28.wireOp",EDGE,"E134");Q0=makeQuery(id+"F31.boolean.opBoolean","SPLIT",EDGE,{"disambiguationData":[TD([makeQuery(id+"F29.opExtrude","SWEPT_FACE",FACE,{"disambiguationData":[OSD([subQ1])]})])],"derivedFrom":makeQuery(id+"F29.opExtrude","CAP_EDGE",EDGE,{"disambiguationData":[OSD([subQ0])],"isStart":false})});}
            var Q1;
            {var subQ0=sQuery(id+"F28.wireOp",EDGE,"E135");var subQ1=sQuery(id+"F28.wireOp",EDGE,"E134");Q1=makeQuery(id+"F31.boolean.opBoolean","SPLIT",EDGE,{"disambiguationData":[TD([makeQuery(id+"F29.opExtrude","SWEPT_FACE",FACE,{"disambiguationData":[OSD([subQ1])]})])],"derivedFrom":makeQuery(id+"F29.opExtrude","CAP_EDGE",EDGE,{"disambiguationData":[OSD([subQ0])],"isStart":false})});}
            var Q2;
            {var subQ0=sQuery(id+"F28.wireOp",EDGE,"E133");var subQ1=sQuery(id+"F28.wireOp",EDGE,"E131");Q2=makeQuery(id+"F31.boolean.opBoolean","SPLIT",EDGE,{"disambiguationData":[TD([makeQuery(id+"F29.opExtrude","SWEPT_FACE",FACE,{"disambiguationData":[OSD([subQ1])]})])],"derivedFrom":makeQuery(id+"F29.opExtrude","CAP_EDGE",EDGE,{"disambiguationData":[OSD([subQ0])],"isStart":false})});}
            var Q3;
            {var subQ0=sQuery(id+"F28.wireOp",EDGE,"E135");var subQ1=sQuery(id+"F28.wireOp",EDGE,"E131");Q3=makeQuery(id+"F31.boolean.opBoolean","SPLIT",EDGE,{"disambiguationData":[TD([makeQuery(id+"F29.opExtrude","SWEPT_FACE",FACE,{"disambiguationData":[OSD([subQ1])]})])],"derivedFrom":makeQuery(id+"F29.opExtrude","CAP_EDGE",EDGE,{"disambiguationData":[OSD([subQ0])],"isStart":false})});}
            var Q4;
            {var subQ0=sQuery(id+"F9.wireOp",EDGE,"E32");var subQ1=makeQuery(id+"F20.boolean.opBoolean","COPY",FACE,{"derivedFrom":makeQuery(id+"F20.opExtrude","SWEPT_FACE",FACE,{"disambiguationData":[OSD([sQuery(id+"F16.wireOp",EDGE,"E53")])]})});var subQ2=sQuery(id+"F9.wireOp",EDGE,"E23");Q4=makeQuery(id+"F23.boolean.opBoolean","SPLIT",EDGE,{"disambiguationData":[TD([subQ1])],"derivedFrom":makeQuery(id+"F12.opExtrude","SWEPT_EDGE",EDGE,{"disambiguationData":[OSD([subQ2,subQ0])]})});}
            var Q5;
            {var subQ0=makeQuery(id+"F20.boolean.opBoolean","COPY",FACE,{"derivedFrom":makeQuery(id+"F20.opExtrude","SWEPT_FACE",FACE,{"disambiguationData":[OSD([sQuery(id+"F16.wireOp",EDGE,"E51")])]})});var subQ1=sQuery(id+"F9.wireOp",EDGE,"E32");var subQ2=sQuery(id+"F9.wireOp",EDGE,"E23");Q5=makeQuery(id+"F23.boolean.opBoolean","SPLIT",EDGE,{"disambiguationData":[TD([subQ0])],"derivedFrom":makeQuery(id+"F12.opExtrude","SWEPT_EDGE",EDGE,{"disambiguationData":[OSD([subQ2,subQ1])]})});}
            var Q6;
            Q6=makeQuery(id+"F12.opExtrude","SWEPT_EDGE",EDGE,{"disambiguationData":[OSD([sQuery(id+"F9.wireOp",EDGE,"E22"),sQuery(id+"F9.wireOp",EDGE,"E23")])]});
            var Q7;
            Q7=makeQuery(id+"F12.opExtrude","SWEPT_EDGE",EDGE,{"disambiguationData":[OSD([sQuery(id+"F9.wireOp",EDGE,"E18"),sQuery(id+"F9.wireOp",EDGE,"E19")])]});
            var Q8;
            Q8=makeQuery(id+"F12.opExtrude","SWEPT_EDGE",EDGE,{"disambiguationData":[OSD([sQuery(id+"F9.wireOp",EDGE,"E20"),sQuery(id+"F9.wireOp",EDGE,"E21")])]});
            var Q9;
            Q9=makeQuery(id+"F12.opExtrude","SWEPT_EDGE",EDGE,{"disambiguationData":[OSD([sQuery(id+"F9.wireOp",EDGE,"E24"),sQuery(id+"F9.wireOp",EDGE,"E25")])]});
            var Q10;
            {var subQ0=sQuery(id+"F9.wireOp",EDGE,"E32");var subQ1=sQuery(id+"F9.wireOp",EDGE,"E24");Q10=makeQuery(id+"F20.boolean.opBoolean","SPLIT",EDGE,{"disambiguationData":[TD([makeQuery(id+"F20.opExtrude","SWEPT_FACE",FACE,{"disambiguationData":[OSD([sQuery(id+"F16.wireOp",EDGE,"E53")])]})])],"derivedFrom":makeQuery(id+"F12.opExtrude","SWEPT_EDGE",EDGE,{"disambiguationData":[OSD([subQ1,subQ0])]})});}
            var Q11;
            {var subQ0=sQuery(id+"F9.wireOp",EDGE,"E32");var subQ1=sQuery(id+"F9.wireOp",EDGE,"E24");Q11=makeQuery(id+"F20.boolean.opBoolean","SPLIT",EDGE,{"disambiguationData":[TD([makeQuery(id+"F20.opExtrude","SWEPT_FACE",FACE,{"disambiguationData":[OSD([sQuery(id+"F16.wireOp",EDGE,"E51")])]})])],"derivedFrom":makeQuery(id+"F12.opExtrude","SWEPT_EDGE",EDGE,{"disambiguationData":[OSD([subQ1,subQ0])]})});}
            fillet(context, id + "F32", {"entities" : qUnion([Q0, Q1, Q2, Q3, Q4, Q5, Q6, Q7, Q8, Q9, Q10, Q11]), "radius" : getVariable(context, 'T') / 2 * mm, "tangentPropagation" : true, "allowEdgeOverflow" : false});
        }
    });
